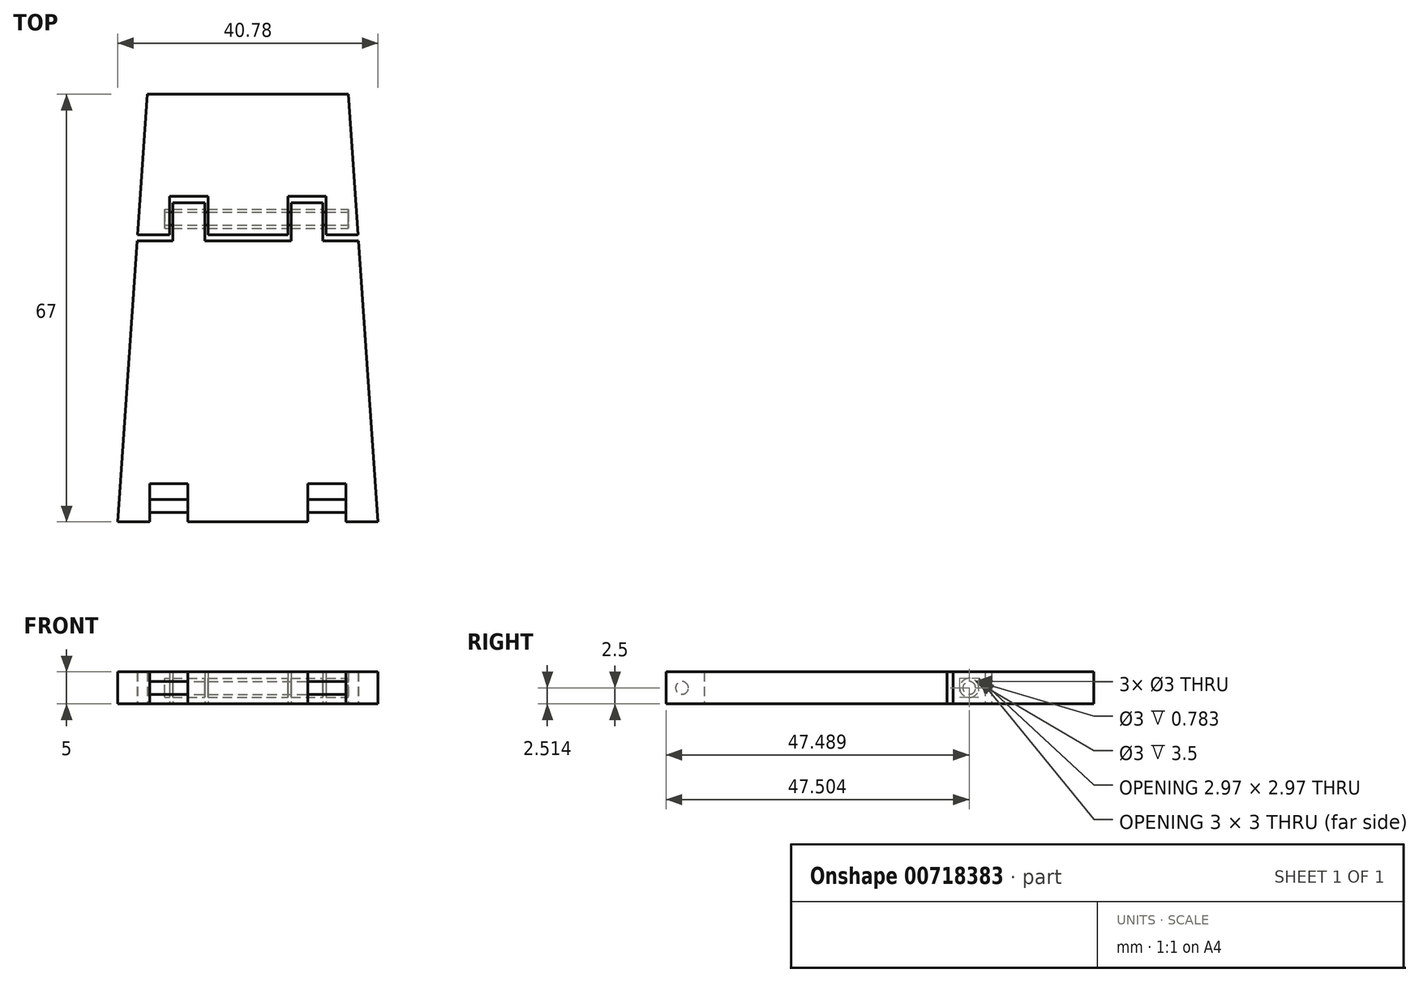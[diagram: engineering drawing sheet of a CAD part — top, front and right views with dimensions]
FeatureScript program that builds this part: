
annotation { "Feature Type Name" : "Feature", "Feature Type Description" : "" }
export const myFeature = defineFeature(function(context is Context, id is Id, definition is map)
    precondition{}
    {
        {
            var Q0;
            Q0=qCreatedBy(makeId("Top.planeOp"),FACE);
            var sketch = newSketch(context, id + "F0", { "sketchPlane" : qUnion([Q0])});
            skLineSegment(sketch, "E0", {"start": v(-17.26, -128.97) * mm, "end": v(-12.26, -128.97) * mm});
            skLineSegment(sketch, "E1", {"start": v(-20.39, -173.97) * mm, "end": v(-15.39, -173.97) * mm});
            skLineSegment(sketch, "E2.top", {"start": v(-12.26, -122.97) * mm, "end": v(-6.26, -122.97) * mm});
            skLineSegment(sketch, "E2.left", {"start": v(-12.26, -128.97) * mm, "end": v(-12.26, -122.97) * mm});
            skLineSegment(sketch, "E2.right", {"start": v(-6.26, -128.97) * mm, "end": v(-6.26, -122.97) * mm});
            skLineSegment(sketch, "E3.top", {"start": v(-15.39, -167.97) * mm, "end": v(-9.39, -167.97) * mm});
            skLineSegment(sketch, "E3.left", {"start": v(-15.39, -173.97) * mm, "end": v(-15.39, -167.97) * mm});
            skLineSegment(sketch, "E3.right", {"start": v(-9.39, -173.97) * mm, "end": v(-9.39, -167.97) * mm});
            skLineSegment(sketch, "E4.MirrorCS", {"start": v(15.39, -167.97) * mm, "end": v(9.39, -167.97) * mm});
            skLineSegment(sketch, "E5.MirrorCS", {"start": v(15.39, -173.97) * mm, "end": v(15.39, -167.97) * mm});
            skLineSegment(sketch, "E6.MirrorCS", {"start": v(9.39, -173.97) * mm, "end": v(9.39, -167.97) * mm});
            skLineSegment(sketch, "E7.MirrorCS", {"start": v(12.26, -128.97) * mm, "end": v(12.26, -122.97) * mm});
            skLineSegment(sketch, "E8.MirrorCS", {"start": v(12.26, -122.97) * mm, "end": v(6.26, -122.97) * mm});
            skLineSegment(sketch, "E9.MirrorCS", {"start": v(6.26, -128.97) * mm, "end": v(6.26, -122.97) * mm});
            skLineSegment(sketch, "E10", {"start": v(-17.33, -129.97) * mm, "end": v(-11.76, -129.97) * mm});
            skLineSegment(sketch, "E11.top", {"start": v(-11.76, -123.97) * mm, "end": v(-6.76, -123.97) * mm});
            skLineSegment(sketch, "E11.left", {"start": v(-11.76, -129.97) * mm, "end": v(-11.76, -123.97) * mm});
            skLineSegment(sketch, "E11.right", {"start": v(-6.76, -129.97) * mm, "end": v(-6.76, -123.97) * mm});
            skLineSegment(sketch, "E12.trimOffspring", {"start": v(-15.73, -106.97) * mm, "end": v(-17.26, -128.97) * mm});
            skLineSegment(sketch, "E13.trimOffspring", {"start": v(15.73, -106.97) * mm, "end": v(17.26, -128.97) * mm});
            skLineSegment(sketch, "E14.MirrorCS", {"start": v(6.76, -129.97) * mm, "end": v(6.76, -123.97) * mm});
            skLineSegment(sketch, "E15.MirrorCS", {"start": v(11.76, -129.97) * mm, "end": v(11.76, -123.97) * mm});
            skLineSegment(sketch, "E16.MirrorCS", {"start": v(11.76, -123.97) * mm, "end": v(6.76, -123.97) * mm});
            skLineSegment(sketch, "E17.trimOffspring", {"start": v(-17.33, -129.97) * mm, "end": v(-20.39, -173.97) * mm});
            skLineSegment(sketch, "E18.trimOffspring", {"start": v(-6.26, -128.97) * mm, "end": v(6.26, -128.97) * mm});
            skLineSegment(sketch, "E19.trimOffspring", {"start": v(-6.76, -129.97) * mm, "end": v(6.76, -129.97) * mm});
            skLineSegment(sketch, "E20.trimOffspring", {"start": v(12.26, -128.97) * mm, "end": v(17.26, -128.97) * mm});
            skLineSegment(sketch, "E21.trimOffspring", {"start": v(17.33, -129.97) * mm, "end": v(20.39, -173.97) * mm});
            skLineSegment(sketch, "E22.trimOffspring", {"start": v(-9.39, -173.97) * mm, "end": v(9.39, -173.97) * mm});
            skLineSegment(sketch, "E23.trimOffspring", {"start": v(15.39, -173.97) * mm, "end": v(20.39, -173.97) * mm});
            skLineSegment(sketch, "E24", {"start": v(11.76, -129.97) * mm, "end": v(17.33, -129.97) * mm});
            skLineSegment(sketch, "E25", {"start": v(-15.73, -106.97) * mm, "end": v(15.73, -106.97) * mm});
            skSolve(sketch);
        }
        {
            var Q0;
            Q0=makeQuery(id+"F0.imprint","IMPRINT",FACE,{"disambiguationData":[TD([[makeQuery(id+"F0.imprint","IMPRINT",EDGE,{"derivedFrom":sQuery(id+"F0.wireOp",EDGE,"sDf46SIC-bLj5-Ihzw-bjZm-QYRj6WgvZJjt")}),1.0]])]});
            var Q1;
            Q1=makeQuery(id+"F0.imprint","IMPRINT",FACE,{"disambiguationData":[TD([[makeQuery(id+"F0.imprint","IMPRINT",EDGE,{"derivedFrom":sQuery(id+"F0.wireOp",EDGE,"E0")}),1.0]])]});
            var Q2;
            Q2=makeQuery(id+"F0.imprint","IMPRINT",FACE,{"disambiguationData":[TD([[makeQuery(id+"F0.imprint","IMPRINT",EDGE,{"derivedFrom":sQuery(id+"F0.wireOp",EDGE,"E1")}),1.0]])]});
            extrude(context, id + "F1", {"entities" : qUnion([Q0, Q1, Q2]), "depth" : 5 * mm, "offsetDistance" : 25 * mm});
        }
        {
            var Q0;
            Q0=makeQuery(id+"F1.opExtrude","SWEPT_FACE",FACE,{"disambiguationData":[OSD([sQuery(id+"F0.wireOp",EDGE,"E15.MirrorCS")])]});
            cPlane(context, id + "F2", {"entities" : qUnion([Q0]), "cplaneType" : CPlaneType.OFFSET, "offset" : 10 * mm, "width" : 150 * mm, "height" : 150 * mm});
        }
        {
            var Q0;
            Q0=qCreatedBy(id+"F2.planeOp",FACE);
            var sketch = newSketch(context, id + "F3", { "sketchPlane" : qUnion([Q0])});
            skCircle(sketch, "E26", {"center": v(-126.47, 2.5) * mm, "radius": 1.5 * mm});
            skCircle(sketch, "E27", {"center": v(-126.47, 2.5) * mm, "radius": 1 * mm});
            skSolve(sketch);
        }
        {
            var Q0;
            Q0=qSketchRegion(id+"F3",true);
            extrude(context, id + "F4", {"entities" : qUnion([Q0]), "operationType" : NewBodyOperationType.REMOVE, "oppositeDirection" : true, "depth" : 34.8 * mm, "offsetDistance" : 25 * mm, "hasSecondDirection" : true, "secondDirectionOppositeDirection" : true, "secondDirectionDepth" : 6 * mm});
        }
        {
            var Q0;
            Q0=makeQuery(id+"F3.imprint","IMPRINT",FACE,{"disambiguationData":[TD([[makeQuery(id+"F3.imprint","IMPRINT",EDGE,{"derivedFrom":sQuery(id+"F3.wireOp",EDGE,"E27")}),1.0]])]});
            extrude(context, id + "F5", {"entities" : qUnion([Q0]), "operationType" : NewBodyOperationType.ADD, "oppositeDirection" : true, "depth" : 35.7 * mm, "offsetDistance" : 25 * mm, "hasSecondDirection" : true, "secondDirectionOppositeDirection" : true, "secondDirectionDepth" : 5.4 * mm});
        }
        {
            var Q0;
            Q0=makeQuery(id+"F1.opExtrude","SWEPT_FACE",FACE,{"disambiguationData":[OSD([sQuery(id+"F0.wireOp",EDGE,"E6.MirrorCS")])]});
            cPlane(context, id + "F6", {"entities" : qUnion([Q0]), "cplaneType" : CPlaneType.OFFSET, "offset" : 20 * mm, "width" : 150 * mm, "height" : 150 * mm});
        }
        {
            var Q0;
            Q0=qCreatedBy(id+"F6.planeOp",FACE);
            var sketch = newSketch(context, id + "F7", { "sketchPlane" : qUnion([Q0])});
            skCircle(sketch, "E28", {"center": v(-171.47, 2.5) * mm, "radius": 1 * mm});
            skSolve(sketch);
        }
        {
            var Q0;
            Q0=makeQuery(id+"F7.imprint","IMPRINT",FACE,{"disambiguationData":[TD([[makeQuery(id+"F7.imprint","IMPRINT",EDGE,{"derivedFrom":sQuery(id+"F7.wireOp",EDGE,"E28")}),1.0]])]});
            extrude(context, id + "F8", {"entities" : qUnion([Q0]), "operationType" : NewBodyOperationType.ADD, "oppositeDirection" : true, "depth" : 47.5 * mm, "offsetDistance" : 25 * mm, "hasSecondDirection" : true, "secondDirectionOppositeDirection" : true, "secondDirectionDepth" : 10.4 * mm});
        }
    });
